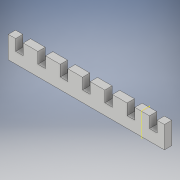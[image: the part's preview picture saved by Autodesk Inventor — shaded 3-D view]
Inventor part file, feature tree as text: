
AUTODESK INVENTOR PART (.ipt)
format: ipt  version: 2017 (Build 210142000, 142)  size: 139,776 bytes
history: native  units: in
note: dims shown in document units (in); Inventor stores cm internally (conversion verified against a paired STEP export)
features: mirror x4, extrude x1, plane x1, sketch x1
ambient origin geometry x8: Origin, YZ Plane, XZ Plane, XY Plane, X Axis, Y Axis, Z Axis, Center Point
bodies: Solid1 (feature_tree)
feature tree (7):
  extrude  "Extrusion1"  Depth=0.2047in
  mirror  "Mirror1"
  mirror  "Mirror2"
  mirror  "Mirror4"
  mirror  "Mirror5"
  plane  "Work Plane3"
  sketch  "Sketch1"  dims[d0=0.5906in d1=0.2047in d2=0.1969in d3=0.1969in d4=0.2953in d5=0.1969in d6=0.0in]
